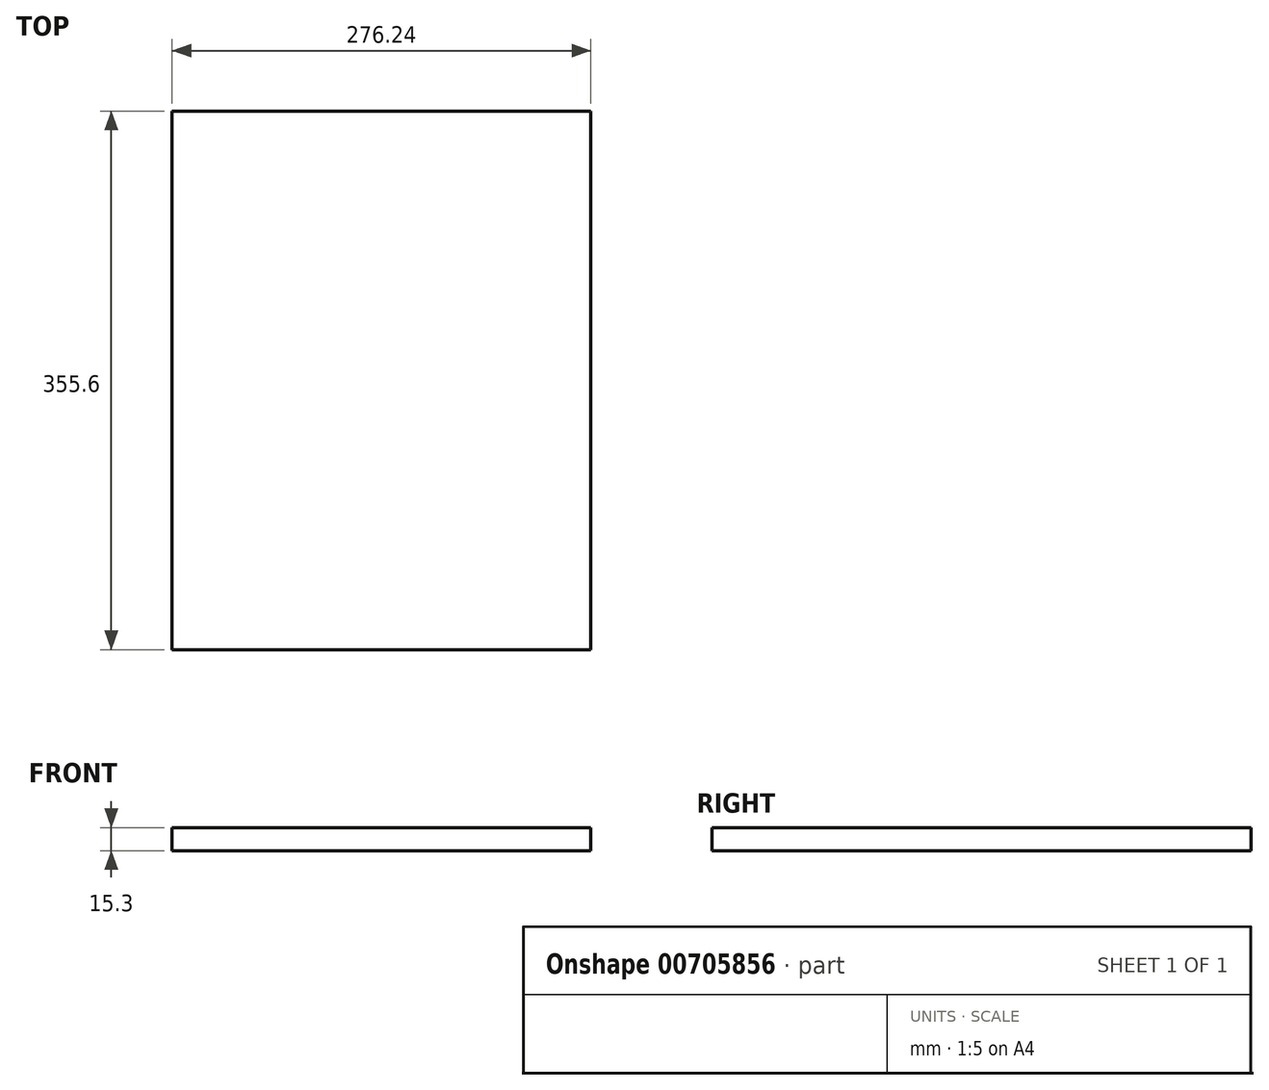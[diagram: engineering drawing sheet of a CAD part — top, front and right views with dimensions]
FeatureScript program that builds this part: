
annotation { "Feature Type Name" : "Feature", "Feature Type Description" : "" }
export const myFeature = defineFeature(function(context is Context, id is Id, definition is map)
    precondition{}
    {
        {
            var Q0;
            Q0=qCreatedBy(makeId("Front.planeOp"),FACE);
            var sketch = newSketch(context, id + "F0", { "sketchPlane" : qUnion([Q0])});
            skLineSegment(sketch, "E0.bottom", {"start": v(-138.12, 7.65) * mm, "end": v(138.12, 7.65) * mm});
            skLineSegment(sketch, "E0.top", {"start": v(-138.12, -7.65) * mm, "end": v(138.12, -7.65) * mm});
            skLineSegment(sketch, "E0.left", {"start": v(-138.12, 7.65) * mm, "end": v(-138.12, -7.65) * mm});
            skLineSegment(sketch, "E0.right", {"start": v(138.12, 7.65) * mm, "end": v(138.12, -7.65) * mm});
            skPoint(sketch, "E0.middle", {"position": v(0, 0) * mm});
            skSolve(sketch);
        }
        {
            var Q0;
            Q0 = qSketchRegion(id + "F0", true);
            extrude(context, id + "F1", {"entities" : qUnion([Q0]), "depth" : 355.6 * mm, "offsetDistance" : 25.4 * mm});
        }
    });
